# Revit family: Faucet-Kitchen-KOHLER-Graze-K-22065_1
name_source: partatom
category: Plumbing Fixtures
revit_build: Autodesk Revit 2017 (Build: 20160225_1515(x64)
units: mm (PartAtom-declared; Revit-internal decimal feet)

## family parameters
Cut with Voids When Loaded = No
Host = Face
OmniClass Number = 23.31.11.00
OmniClass Title = Faucets
Part Type = Normal
Room Calculation Point = No
Round Connector Dimension = Use Diameter
Shared = No

## types (4) — shared parameters
ADA Compliant = Yes
Assembly Code = D2010
CW Connection = Yes
Cold Water Inlet = Cold Water Inlet
Date Modified = 06/30/2020
Default Elevation = 36"
Description = Bar sink faucet with swing spout
Drain Included = No
Faucet Hole Spacing = 0"
Flow Rate = 2 GPM
HW Connection = Yes
Handle Clearance = 3 1/16"
Height = 13 3/4"
Hot Water Inlet = Hot Water Inlet
Length = 8 1/8"
Manufacturer = KOHLER Co.
Master Format 2014 = 22 41 39
Master Format 2014 Name = Residential Faucets, Supplies, and Trim
Material = Premium metal construction
Pressure = 60.00 psi
Product Documentation Link = https://www.us.kohler.com
Product Name = Graze
Product Page URL = http://www.us.kohler.com
Spout Reach = 8 1/8"
URL = https://www.us.kohler.com
Vent Connection = No
Waste Connection = No
Waste Water Outlet = Waste Water Outlet
WaterSense Certified = No
Width = 2 3/8"

## per-type parameters (varying)
| type | Finish | Model | Type |
| CP- Polished Chrome | Kohler-Metal-CP-Polished_Chrome | K-22065-CP | 1 |
| VS- Vibrant Stainless | Kohler-Metal-VS-Vibrant_Stainless | K-22065-VS | 2 |
| BL- Matte Black | Kohler-Metal-BL-Matte_Black | K-22065-BL | 3 |
| 2MB-Vibrant Brushed Moderne Brass | Kohler-Metal-2MB-Vibrant_Brushed_Moderne_Brass | K-22065-2MB | 4 |

## geometry (parser evidence)
native form markers: Sweep x4
no freeform markers — native parametric forms only
